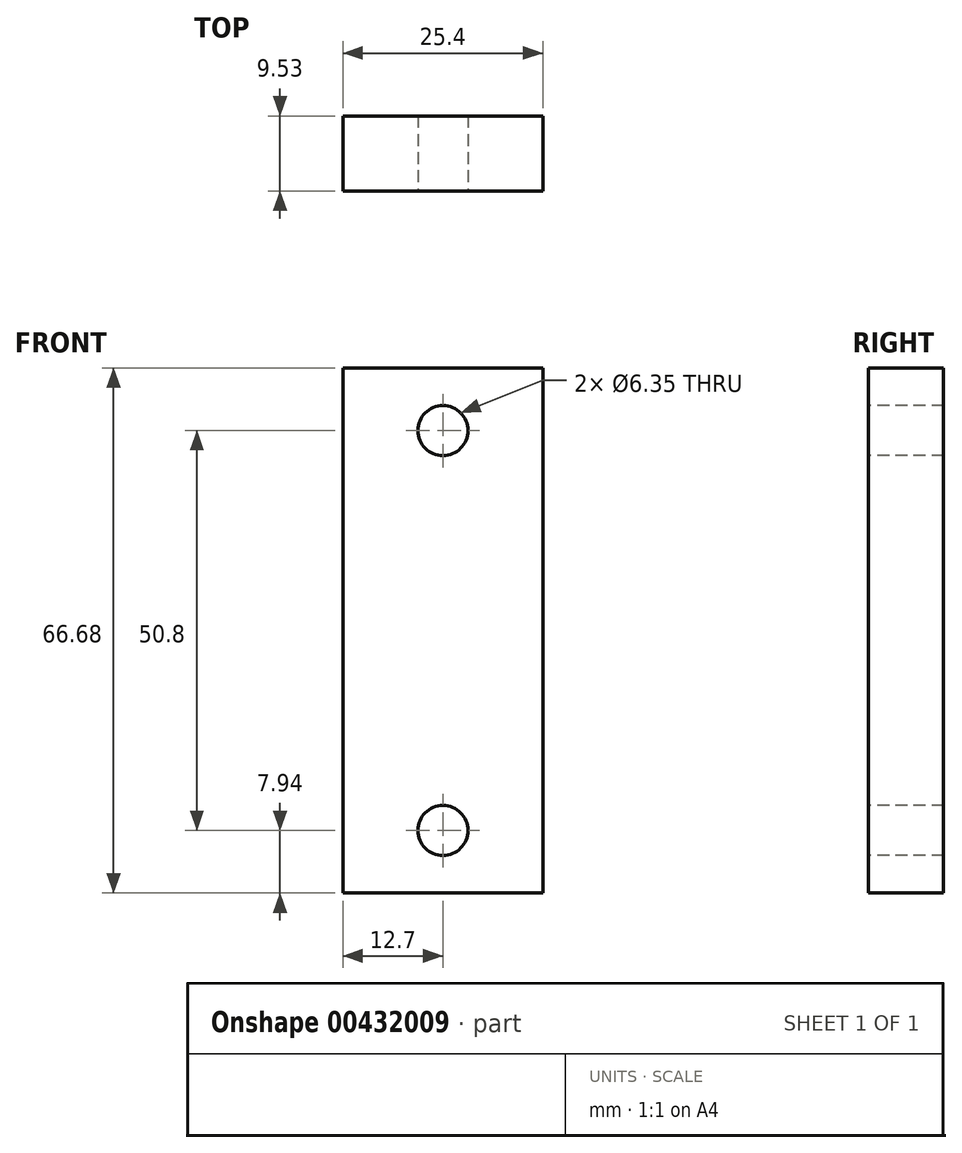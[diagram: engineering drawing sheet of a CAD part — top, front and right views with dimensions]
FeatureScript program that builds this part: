
annotation { "Feature Type Name" : "Feature", "Feature Type Description" : "" }
export const myFeature = defineFeature(function(context is Context, id is Id, definition is map)
    precondition{}
    {
        {
            var Q0;
            Q0=qCreatedBy(makeId("Front.planeOp"),FACE);
            var sketch = newSketch(context, id + "F0", { "sketchPlane" : qUnion([Q0])});
            skLineSegment(sketch, "E0.bottom", {"start": v(-12.7, 33.34) * mm, "end": v(12.7, 33.34) * mm});
            skLineSegment(sketch, "E0.top", {"start": v(-12.7, -33.34) * mm, "end": v(12.7, -33.34) * mm});
            skLineSegment(sketch, "E0.left", {"start": v(-12.7, 33.34) * mm, "end": v(-12.7, -33.34) * mm});
            skLineSegment(sketch, "E0.right", {"start": v(12.7, 33.34) * mm, "end": v(12.7, -33.34) * mm});
            skPoint(sketch, "E0.middle", {"position": v(0, 0) * mm});
            skSolve(sketch);
        }
        {
            var Q0;
            Q0 = qSketchRegion(id + "F0", true);
            extrude(context, id + "F1", {"entities" : qUnion([Q0]), "depth" : 9.52 * mm});
        }
        {
            var Q0;
            Q0=makeQuery(id+"F1.opExtrude","CAP_FACE",FACE,{"disambiguationData":[OSD([sQuery(id+"F0.wireOp",EDGE,"E0.bottom"),sQuery(id+"F0.wireOp",EDGE,"E0.top"),sQuery(id+"F0.wireOp",EDGE,"E0.left"),sQuery(id+"F0.wireOp",EDGE,"E0.right")])],"isStart":false});
            var sketch = newSketch(context, id + "F2", { "sketchPlane" : qUnion([Q0])});
            skCircle(sketch, "E1", {"center": v(0, 25.4) * mm, "radius": 3.18 * mm});
            skCircle(sketch, "E2.MirrorC", {"center": v(0, -25.4) * mm, "radius": 3.18 * mm});
            skSolve(sketch);
        }
        {
            var Q0;
            Q0 = qSketchRegion(id + "F2", true);
            extrude(context, id + "F3", {"entities" : qUnion([Q0]), "operationType" : NewBodyOperationType.REMOVE, "endBound" : BoundingType.THROUGH_ALL, "oppositeDirection" : true, "depth" : 25.4 * mm});
        }
    });
